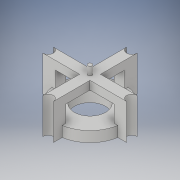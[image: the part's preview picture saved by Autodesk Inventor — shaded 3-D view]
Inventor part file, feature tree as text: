
AUTODESK INVENTOR PART (.ipt)
format: ipt  version: 2019 (Build 230136000, 136)  size: 198,144 bytes
history: native  units: mm
features: extrude x5, sketch x5
ambient origin geometry x8: Origin, YZ Plane, XZ Plane, XY Plane, X Axis, Y Axis, Z Axis, Center Point
bodies: Body1 (feature_tree)
feature tree (10):
  extrude  "Extrusion15"  Depth=32.0mm
  extrude  "Extrusion16"  Depth=2.5mm
  extrude  "Extrusion17"  Depth=2.5mm
  extrude  "Extrusion18"  Depth=5.0mm TaperAngle=0.0deg
  extrude  "Extrusion19"  Depth=4.0mm
  sketch  "Sketch14"  dims[d4=30.0mm d48=32.0mm d86=32.0mm]
  sketch  "Sketch15"  dims[d87=2.5mm d88=2.5mm]
  sketch  "Sketch16"  dims[d89=2.5mm d90=2.5mm]
  sketch  "Sketch17"  dims[d91=15.0mm d92=5.0mm d93=0.0mm]
  sketch  "Sketch18"  dims[d94=17.0mm d95=30.0mm d96=1.0mm d97=0.0mm d98=8.0mm d99=0.0mm d100=4.0mm d101=0.0mm d102=2.0mm d103=4.0mm d104=0.0mm]
